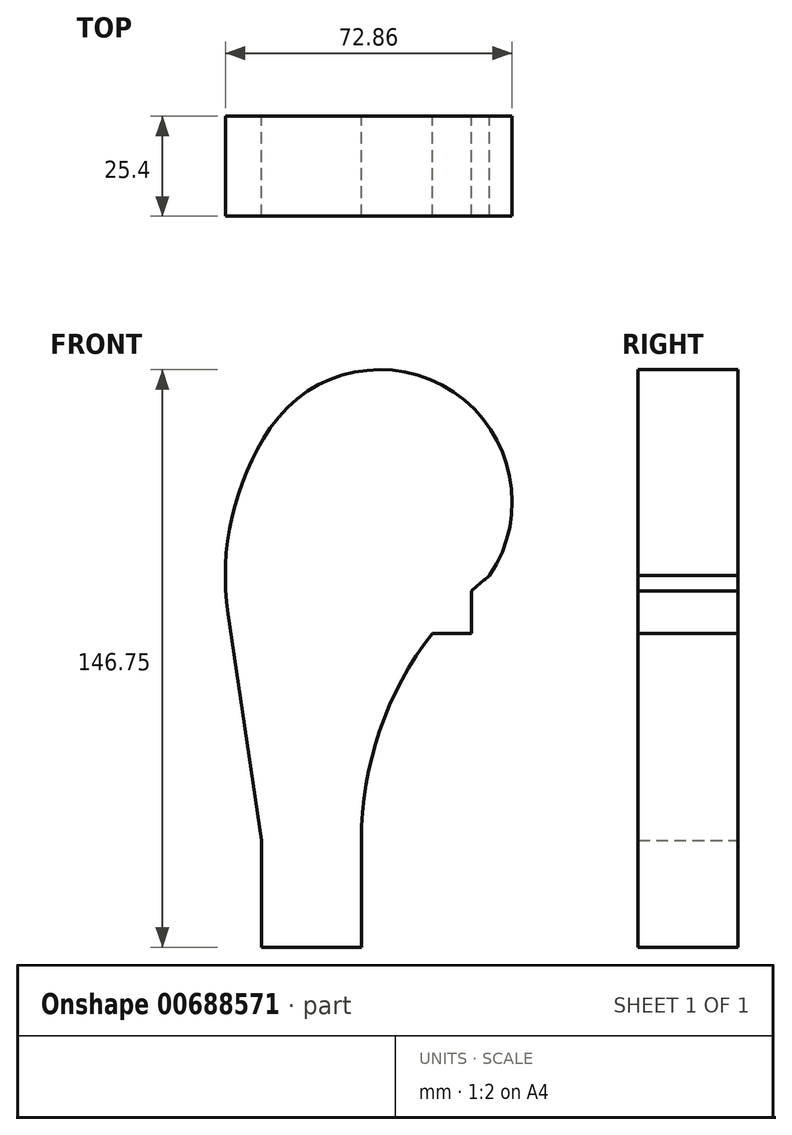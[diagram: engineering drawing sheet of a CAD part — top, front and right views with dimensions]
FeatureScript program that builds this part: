
annotation { "Feature Type Name" : "Feature", "Feature Type Description" : "" }
export const myFeature = defineFeature(function(context is Context, id is Id, definition is map)
    precondition{}
    {
        {
            var Q0;
            Q0=qCreatedBy(makeId("Front.planeOp"),FACE);
            var sketch = newSketch(context, id + "F0", { "sketchPlane" : qUnion([Q0])});
            skLineSegment(sketch, "E0.bottom", {"start": v(12.7, -13.6) * mm, "end": v(-12.7, -13.6) * mm});
            skLineSegment(sketch, "E0.top", {"start": v(12.7, 13.6) * mm, "end": v(-12.7, 13.6) * mm});
            skLineSegment(sketch, "E0.left", {"start": v(12.7, -13.6) * mm, "end": v(12.7, 13.6) * mm});
            skLineSegment(sketch, "E0.right", {"start": v(-12.7, -13.6) * mm, "end": v(-12.7, 13.6) * mm});
            skPoint(sketch, "E0.middle", {"position": v(0, 0) * mm});
            skLineSegment(sketch, "E1.bottom", {"start": v(40.66, 66.17) * mm, "end": v(21.61, 66.17) * mm});
            skLineSegment(sketch, "E1.top", {"start": v(40.66, 94.75) * mm, "end": v(21.61, 94.75) * mm});
            skLineSegment(sketch, "E1.left", {"start": v(40.66, 66.17) * mm, "end": v(40.66, 94.75) * mm});
            skLineSegment(sketch, "E1.right", {"start": v(21.61, 66.17) * mm, "end": v(21.61, 94.75) * mm});
            skPoint(sketch, "E1.middle", {"position": v(31.14, 80.46) * mm});
            skLineSegment(sketch, "E2", {"start": v(-12.7, 13.6) * mm, "end": v(-21.17, 71.08) * mm});
            skArc(sketch, "E3", {"start": v(-21.17, 71.08) * mm, "mid": v(-20.23, 95.7) * mm, "end": v(-10.47, 118.31) * mm});
            skArc(sketch, "E4", {"start": v(-10.47, 118.31) * mm, "mid": v(36.12, 127.46) * mm, "end": v(45.27, 80.86) * mm});
            skArc(sketch, "E5", {"start": v(12.7, 13.6) * mm, "mid": v(21.27, 50.96) * mm, "end": v(45.27, 80.86) * mm});
            skSolve(sketch);
        }
        {
            var Q0;
            Q0 = qSketchRegion(id + "F0", true);
            extrude(context, id + "F1", {"entities" : qUnion([Q0]), "depth" : 25.4 * mm, "offsetDistance" : 25.4 * mm});
        }
    });
